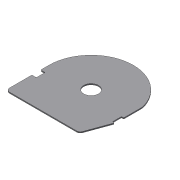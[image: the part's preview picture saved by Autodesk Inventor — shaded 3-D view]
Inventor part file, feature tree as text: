
AUTODESK INVENTOR PART (.ipt)
format: ipt  version: 2015 (Build 190159000, 159)  size: 131,584 bytes
history: native  units: mm
features: fillet x3, extrude x1, sketch x1
ambient origin geometry x8: Origin, YZ Plane, XZ Plane, XY Plane, X Axis, Y Axis, Z Axis, Center Point
bodies: Solid1 (feature_tree)
feature tree (5):
  extrude  "Extrusion1"  Depth=57.0mm
  fillet  "Fillet1"  Radius=20.0mm
  fillet  "Fillet2"  Radius=99.0mm
  fillet  "Fillet3"  Radius=6.0mm
  sketch  "Sketch1"  dims[d0=20.0mm d1=57.0mm d2=20.0mm d3=99.0mm d4=6.0mm d5=19.198622mm d6=3.0mm d7=12.0mm d8=58.0mm d9=12.0mm d10=55.0mm d11=47.0mm d12=1.5mm d13=0.0mm d14=0.5mm d15=1.0mm d16=5.0mm]
